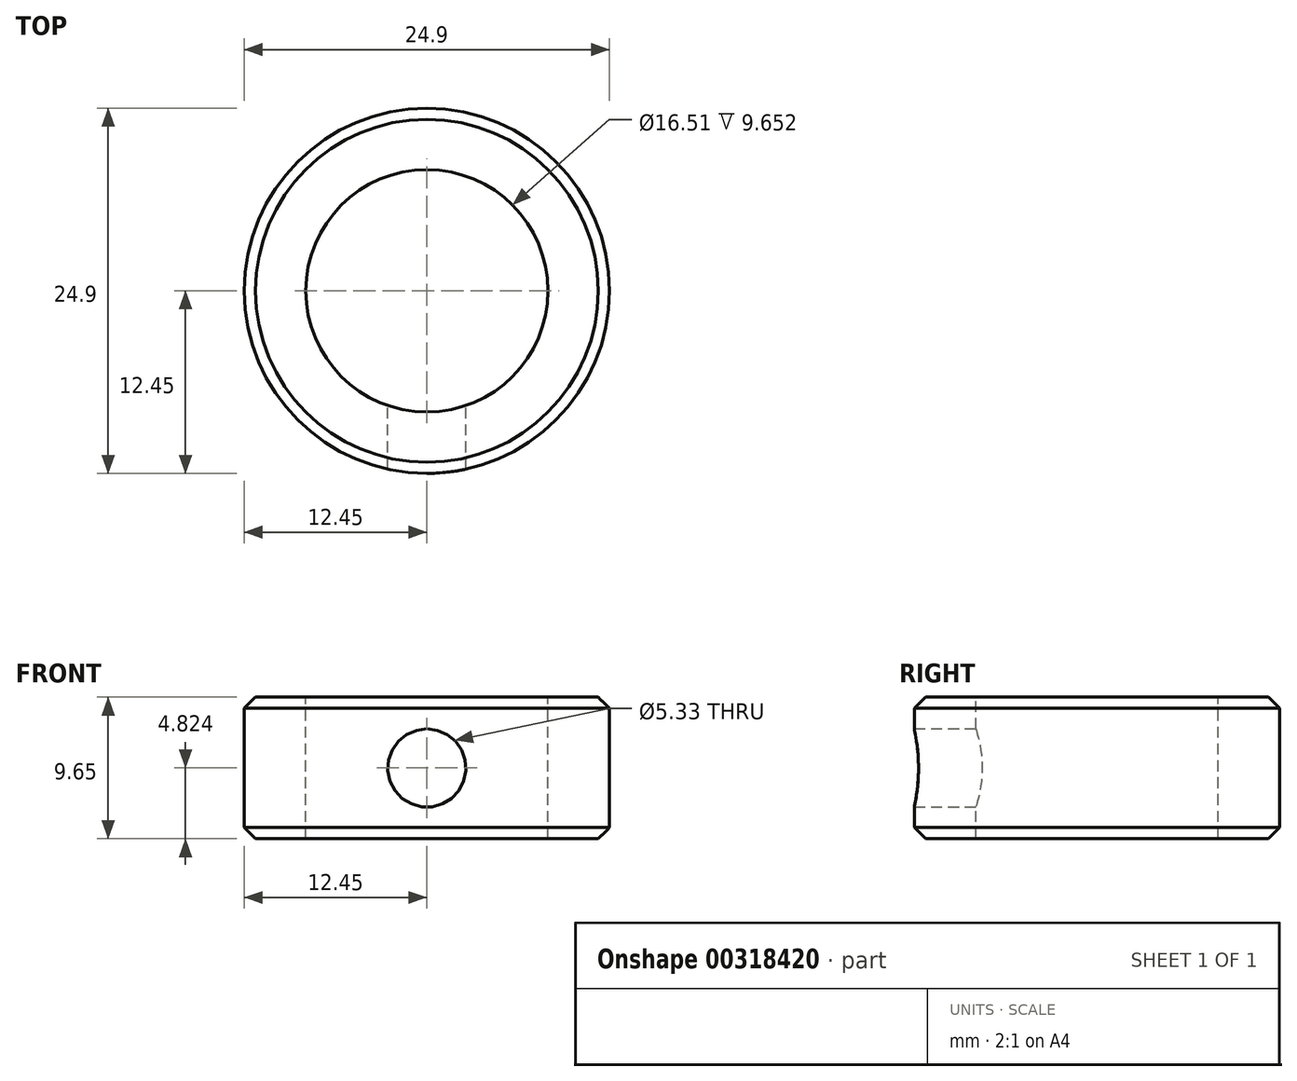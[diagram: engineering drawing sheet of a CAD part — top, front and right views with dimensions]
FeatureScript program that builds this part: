
annotation { "Feature Type Name" : "Feature", "Feature Type Description" : "" }
export const myFeature = defineFeature(function(context is Context, id is Id, definition is map)
    precondition{}
    {
        {
            var Q0;
            Q0=qCreatedBy(makeId("Top.planeOp"),FACE);
            var sketch = newSketch(context, id + "F0", { "sketchPlane" : qUnion([Q0])});
            skCircle(sketch, "E0", {"center": v(0, 0) * mm, "radius": 12.45 * mm});
            skSolve(sketch);
        }
        {
            var Q0;
            Q0 = qSketchRegion(id + "F0", true);
            var Q1;
            Q1 = qSketchRegion(id + "F2", true);
            extrude(context, id + "F1", {"entities" : qUnion([Q0, Q1]), "oppositeDirection" : true, "depth" : 9.65 * mm});
        }
        {
            var Q0;
            Q0=qCreatedBy(makeId("Top.planeOp"),FACE);
            var sketch = newSketch(context, id + "F2", { "sketchPlane" : qUnion([Q0])});
            skPoint(sketch, "E1", {"position": v(0, 0) * mm});
            skSolve(sketch);
        }
        {
            var Q0;
            Q0=sQuery(id+"F2.wireOp",VERTEX,"E1");
            var Q1;
            Q1=makeQuery(id+"F1.opExtrude","SWEPT_BODY",BODY,{"disambiguationData":[OSD([sQuery(id+"F0.wireOp",EDGE,"E0")])]});
            hole(context, id + "F3", {"style" : HoleStyle.SIMPLE, "endStyle" : HoleEndStyle.THROUGH, "holeDiameter" : 16.5 * mm, "tappedDepth" : 12.7 * mm, "tapClearance" : 3, "locations" : qUnion([Q0]), "scope" : qUnion([Q1])});
        }
        {
            var Q0;
            Q0=qCreatedBy(makeId("Front.planeOp"),FACE);
            var sketch = newSketch(context, id + "F4", { "sketchPlane" : qUnion([Q0])});
            skPoint(sketch, "E2", {"position": v(0, -4.83) * mm});
            skSolve(sketch);
        }
        {
            var Q0;
            Q0=sQuery(id+"F4.wireOp",VERTEX,"E2");
            var Q1;
            Q1=makeQuery(id+"F1.opExtrude","SWEPT_BODY",BODY,{"disambiguationData":[OSD([sQuery(id+"F0.wireOp",EDGE,"E0")])]});
            hole(context, id + "F5", {"style" : HoleStyle.SIMPLE, "endStyle" : HoleEndStyle.THROUGH, "oppositeDirection" : true, "holeDiameter" : 5.33 * mm, "tappedDepth" : 12.7 * mm, "tapClearance" : 3, "locations" : qUnion([Q0]), "scope" : qUnion([Q1])});
        }
        {
            var Q0;
            Q0=makeQuery(id+"F1.opExtrude","CAP_EDGE",EDGE,{"disambiguationData":[OSD([sQuery(id+"F0.wireOp",EDGE,"E0")])],"isStart":true});
            var Q1;
            Q1=makeQuery(id+"F3.hole-0.boolean.opBoolean","COPY",EDGE,{"derivedFrom":makeQuery(id+"F3.hole-0.opRevolve","SWEPT_EDGE",EDGE,{"disambiguationData":[OSD([sQuery(id+"F3.hole-0.sketch.wireOp",EDGE,"core_line_2"),sQuery(id+"F3.hole-0.sketch.wireOp",EDGE,"core_line_3")])]})});
            var Q2;
            Q2=makeQuery(id+"F1.opExtrude","CAP_EDGE",EDGE,{"disambiguationData":[OSD([sQuery(id+"F0.wireOp",EDGE,"E0")])],"isStart":false});
            var Q3;
            Q3=makeQuery(id+"F5.hole-0.boolean.opBoolean","INTERSECT",EDGE,{"derivedFrom":[makeQuery(id+"F1.opExtrude","SWEPT_FACE",FACE,{"disambiguationData":[OSD([sQuery(id+"F0.wireOp",EDGE,"E0")])]}),makeQuery(id+"F5.hole-0.opRevolve","SWEPT_FACE",FACE,{"disambiguationData":[OSD([sQuery(id+"F5.hole-0.sketch.wireOp",EDGE,"core_line_2")])]})]});
            var Q4;
            Q4=makeQuery(id+"F3.hole-0.boolean.opBoolean","INTERSECT",EDGE,{"derivedFrom":[makeQuery(id+"F1.opExtrude","CAP_FACE",FACE,{"disambiguationData":[OSD([sQuery(id+"F0.wireOp",EDGE,"E0")])],"isStart":false}),makeQuery(id+"F3.hole-0.opRevolve","SWEPT_FACE",FACE,{"disambiguationData":[OSD([sQuery(id+"F3.hole-0.sketch.wireOp",EDGE,"core_line_2")])]})]});
            chamfer(context, id + "F6", {"entities" : qUnion([Q0, Q1, Q2, Q3, Q4]), "width" : 0.76 * mm, "tangentPropagation" : true});
        }
    });
